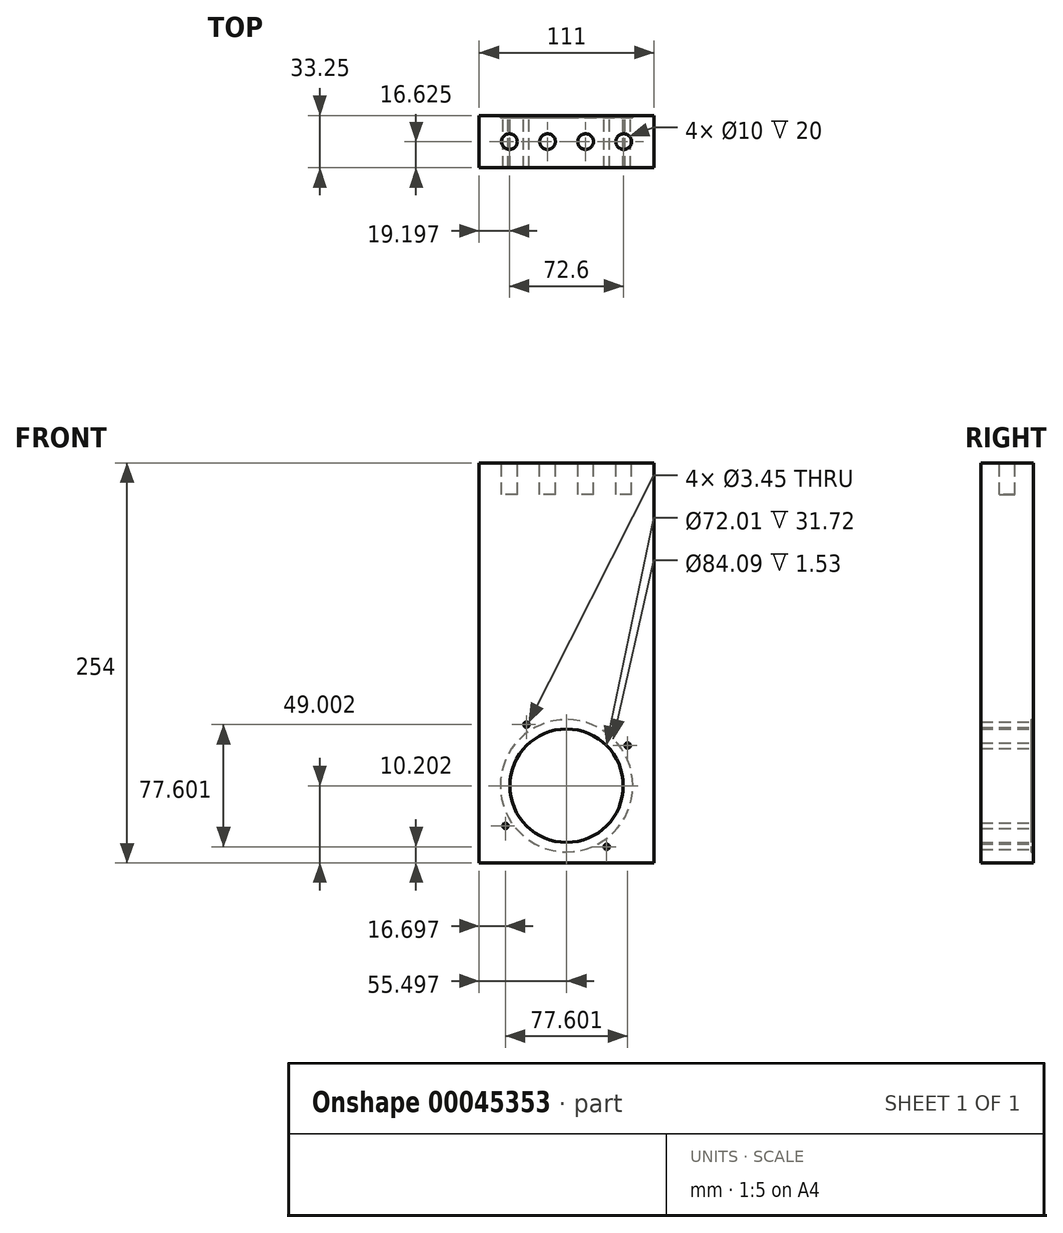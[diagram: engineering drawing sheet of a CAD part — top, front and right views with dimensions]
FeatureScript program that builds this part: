
annotation { "Feature Type Name" : "Feature", "Feature Type Description" : "" }
export const myFeature = defineFeature(function(context is Context, id is Id, definition is map)
    precondition{}
    {
        {
            var Q0;
            Q0=qCreatedBy(makeId("Front.planeOp"),FACE);
            var sketch = newSketch(context, id + "F0", { "sketchPlane" : qUnion([Q0])});
            skLineSegment(sketch, "E0.bottom", {"start": v(-56.76, 170.1) * mm, "end": v(54.24, 170.1) * mm});
            skLineSegment(sketch, "E0.top", {"start": v(-56.76, -83.9) * mm, "end": v(54.24, -83.9) * mm});
            skLineSegment(sketch, "E0.left", {"start": v(-56.76, 170.1) * mm, "end": v(-56.76, -83.9) * mm});
            skLineSegment(sketch, "E0.right", {"start": v(54.24, 170.1) * mm, "end": v(54.24, -83.9) * mm});
            skCircle(sketch, "E1", {"center": v(-1.26, -34.9) * mm, "radius": 36 * mm});
            skCircle(sketch, "E2", {"center": v(-26.76, 3.9) * mm, "radius": 1.73 * mm});
            skCircle(sketch, "E3.1.0", {"center": v(-40.06, -60.4) * mm, "radius": 1.73 * mm});
            skCircle(sketch, "E3.2.0", {"center": v(24.24, -73.7) * mm, "radius": 1.73 * mm});
            skCircle(sketch, "E3.3.0", {"center": v(37.54, -9.4) * mm, "radius": 1.73 * mm});
            skSolve(sketch);
        }
        {
            var Q0;
            Q0 = qSketchRegion(id + "F0", true);
            extrude(context, id + "F1", {"entities" : qUnion([Q0]), "depth" : 33.25 * mm});
        }
        {
            var Q0;
            Q0=makeQuery(id+"F1.opExtrude","CAP_FACE",FACE,{"disambiguationData":[OSD([sQuery(id+"F0.wireOp",EDGE,"E0.bottom"),sQuery(id+"F0.wireOp",EDGE,"E0.top"),sQuery(id+"F0.wireOp",EDGE,"E0.left"),sQuery(id+"F0.wireOp",EDGE,"E0.right"),sQuery(id+"F0.wireOp",EDGE,"E1"),sQuery(id+"F0.wireOp",EDGE,"E2"),sQuery(id+"F0.wireOp",EDGE,"E3.1.0"),sQuery(id+"F0.wireOp",EDGE,"E3.2.0"),sQuery(id+"F0.wireOp",EDGE,"E3.3.0")])],"isStart":true});
            var sketch = newSketch(context, id + "F2", { "sketchPlane" : qUnion([Q0])});
            skCircle(sketch, "E4", {"center": v(1.26, -34.9) * mm, "radius": 42.05 * mm});
            skSolve(sketch);
        }
        {
            var Q0;
            Q0 = qSketchRegion(id + "F2", true);
            extrude(context, id + "F3", {"entities" : qUnion([Q0]), "operationType" : NewBodyOperationType.REMOVE, "oppositeDirection" : true, "depth" : 1.53 * mm});
        }
        {
            var Q0;
            Q0=makeQuery(id+"F1.opExtrude","SWEPT_FACE",FACE,{"disambiguationData":[OSD([sQuery(id+"F0.wireOp",EDGE,"E0.bottom")])]});
            var sketch = newSketch(context, id + "F4", { "sketchPlane" : qUnion([Q0])});
            skCircle(sketch, "E5", {"center": v(-37.56, -16.63) * mm, "radius": 5 * mm});
            skCircle(sketch, "E6.1.0.0", {"center": v(-13.36, -16.62) * mm, "radius": 5 * mm});
            skCircle(sketch, "E6.2.0.0", {"center": v(10.84, -16.63) * mm, "radius": 5 * mm});
            skCircle(sketch, "E6.3.0.0", {"center": v(35.04, -16.63) * mm, "radius": 5 * mm});
            skLineSegment(sketch, "E6.direction1", {"start": v(-37.56, -16.63) * mm, "end": v(-13.36, -16.63) * mm, "construction": true});
            skSolve(sketch);
        }
        {
            var Q0;
            Q0 = qSketchRegion(id + "F4", true);
            extrude(context, id + "F5", {"entities" : qUnion([Q0]), "operationType" : NewBodyOperationType.REMOVE, "oppositeDirection" : true, "depth" : 20 * mm});
        }
    });
